# Revit family: 206_29e31480bb2d47abb0422ca2fa4a8b
name_source: partatom
category: Duct Accessories
revit_build: Autodesk Revit 2018 (Build: 20170223_1515(x64)
units: mm (PartAtom-declared; Revit-internal decimal feet)

## family parameters
Always vertical = Yes
Cut with Voids When Loaded = No
Part Type = Breaks Into
Round Connector Dimension = Use Diameter
Shared = No
Work Plane-Based = No

## types (5) — shared parameters
CAT0 = Yes
Description = Socket sound absorber DSS
H2D = 305 mm  [stored 1.00066 ft]
L2D = 600 mm  [stored 1.9685 ft]
Manufacturer = Flexit
SB = 30 mm  [stored 0.0984252 ft]
SH = 30 mm  [stored 0.0984252 ft]
URL = www.flexit.no
W2D = 305 mm  [stored 1.00066 ft]
X1 = 2 mm  [stored 0.00656168 ft]
magiPartTypeId = 206
magiProductFamilyId = 29e31480bb2d47abb0422ca2fa4a8b

## per-type parameters (varying)
| type | A | B | B1 | BT2 | H | H1 | HT2 | L | L1 | LT2 | magiProductId |
| 114683 | 457 mm  [stored 1.49934 ft] | 245 mm | 305 mm  [stored 1.00066 ft] | 123 mm | 245 mm | 305 mm  [stored 1.00066 ft] | 123 mm | 600 mm  [stored 1.9685 ft] | 598 mm | 300 mm  [stored 0.984252 ft] | 916748ccfea243558d7afc867c8a80 |
| 114684 | 557 mm | 330 mm | 390 mm | 165 mm  [stored 0.541339 ft] | 330 mm | 390 mm | 165 mm  [stored 0.541339 ft] | 600 mm  [stored 1.9685 ft] | 598 mm | 300 mm  [stored 0.984252 ft] | 00dc7afdbad14d90b5d759112cedc5 |
| 114685 | 757 mm | 450 mm | 510 mm | 225 mm | 450 mm | 510 mm | 225 mm | 601 mm  [stored 1.97178 ft] | 599 mm  [stored 1.96522 ft] | 301 mm | b255b7a54a094041b2e6d1f141cc35 |
| 114686 | 815 mm | 535 mm | 595 mm | 268 mm | 535 mm | 595 mm | 268 mm | 601 mm  [stored 1.97178 ft] | 599 mm  [stored 1.96522 ft] | 301 mm | 960018eba8f24a52b7aac8e914885a |
| 114687 | 1097 mm  [stored 3.59908 ft] | 750 mm | 810 mm  [stored 2.65748 ft] | 375 mm  [stored 1.23031 ft] | 750 mm | 810 mm  [stored 2.65748 ft] | 375 mm  [stored 1.23031 ft] | 601 mm  [stored 1.97178 ft] | 599 mm  [stored 1.96522 ft] | 301 mm | c0763f82e7f4410bae7b09cf673c0f |

note: column(s) folded — value = type name in every type: MC Product Code

note: [stored X ft] marks values corroborated as IEEE doubles in the binary element streams (Revit-internal decimal feet)

## geometry (parser evidence)
native form markers: Sweep x2
no freeform markers — native parametric forms only
